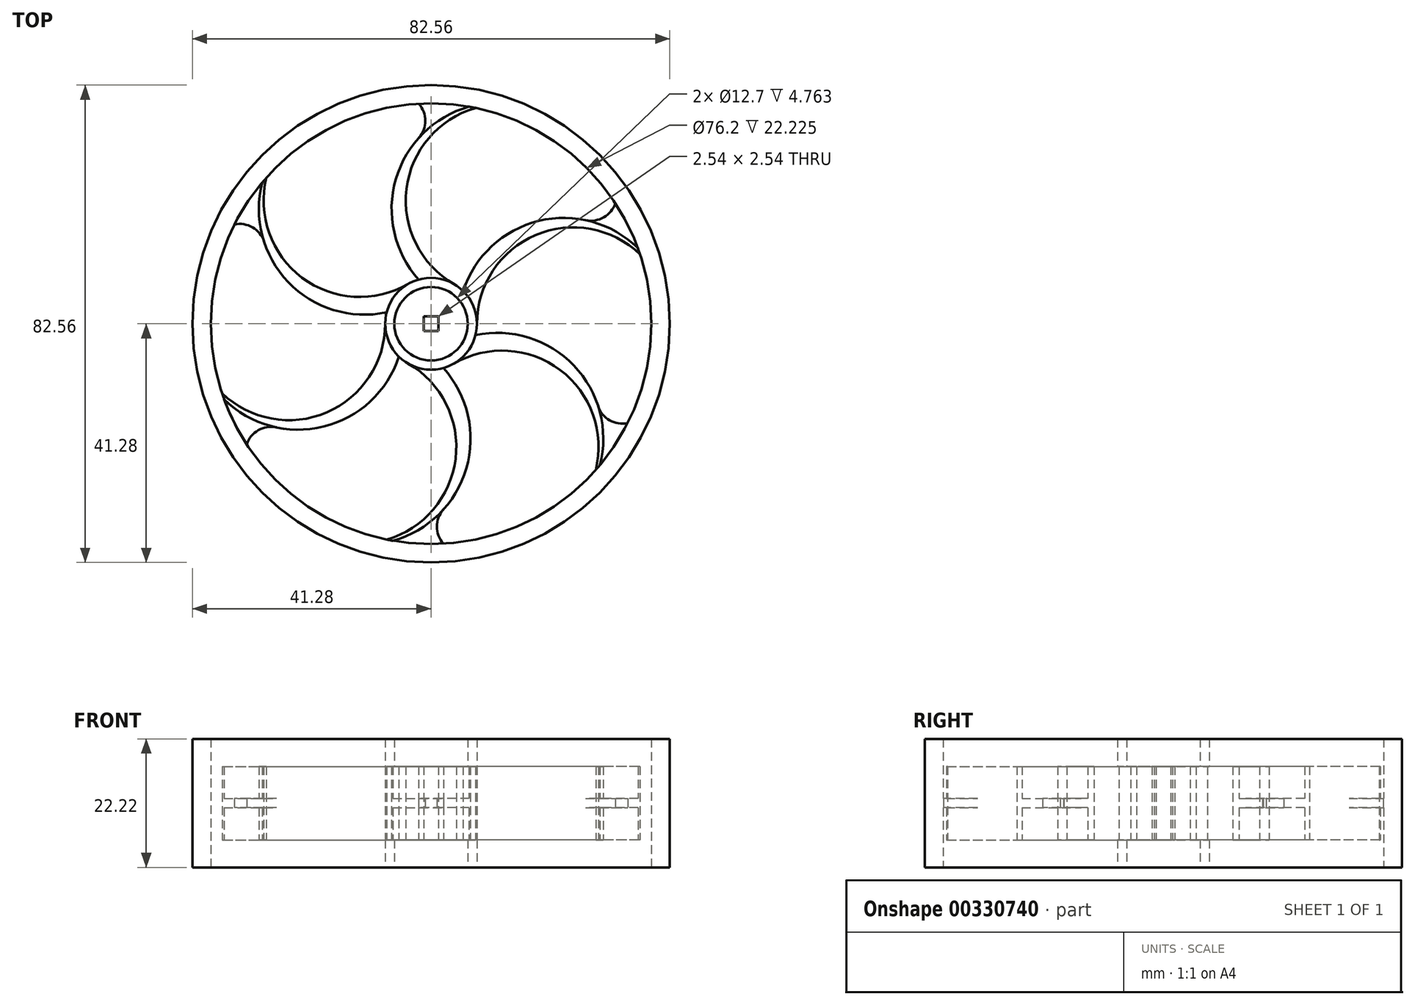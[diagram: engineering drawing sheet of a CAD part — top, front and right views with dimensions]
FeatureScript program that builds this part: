
annotation { "Feature Type Name" : "Feature", "Feature Type Description" : "" }
export const myFeature = defineFeature(function(context is Context, id is Id, definition is map)
    precondition{}
    {
        {
            var Q0;
            Q0=qCreatedBy(makeId("Top.planeOp"),FACE);
            var sketch = newSketch(context, id + "F0", { "sketchPlane" : qUnion([Q0])});
            skCircle(sketch, "E0", {"center": v(0, 0) * mm, "radius": 50.8 * mm});
            skCircle(sketch, "E1", {"center": v(0, 0) * mm, "radius": 41.28 * mm});
            skCircle(sketch, "E2", {"center": v(0, 0) * mm, "radius": 7.94 * mm});
            skLineSegment(sketch, "E3.bottom", {"start": v(-1.27, 1.27) * mm, "end": v(1.27, 1.27) * mm});
            skLineSegment(sketch, "E3.top", {"start": v(-1.27, -1.27) * mm, "end": v(1.27, -1.27) * mm});
            skLineSegment(sketch, "E3.left", {"start": v(-1.27, 1.27) * mm, "end": v(-1.27, -1.27) * mm});
            skLineSegment(sketch, "E3.right", {"start": v(1.27, 1.27) * mm, "end": v(1.27, -1.27) * mm});
            skLineSegment(sketch, "E4", {"start": v(-7.94, 0) * mm, "end": v(-41.28, 0) * mm, "construction": true});
            skLineSegment(sketch, "E5", {"start": v(7.94, 0) * mm, "end": v(41.28, 0) * mm, "construction": true});
            skArc(sketch, "E6", {"start": v(-41.28, 0) * mm, "mid": v(-24.6, -16.67) * mm, "end": v(-7.94, 0) * mm});
            skArc(sketch, "E7.1.0", {"start": v(-20.64, -35.75) * mm, "mid": v(2.13, -29.64) * mm, "end": v(-3.97, -6.87) * mm});
            skArc(sketch, "E7.2.0", {"start": v(20.64, -35.75) * mm, "mid": v(26.74, -12.98) * mm, "end": v(3.97, -6.87) * mm});
            skArc(sketch, "E7.3.0", {"start": v(41.28, 0) * mm, "mid": v(24.6, 16.67) * mm, "end": v(7.94, 0) * mm});
            skArc(sketch, "E7.4.0", {"start": v(20.64, 35.75) * mm, "mid": v(-2.13, 29.64) * mm, "end": v(3.97, 6.87) * mm});
            skArc(sketch, "E7.5.0", {"start": v(-20.64, 35.75) * mm, "mid": v(-26.74, 12.98) * mm, "end": v(-3.97, 6.87) * mm});
            skPoint(sketch, "E8", {"position": v(-2.13, 7.65) * mm});
            skPoint(sketch, "E8.positionSnap0", {"position": v(-2.13, 29.64) * mm});
            skPoint(sketch, "E9.1.0", {"position": v(-7.69, 1.98) * mm});
            skPoint(sketch, "E9.2.0", {"position": v(-5.56, -5.67) * mm});
            skPoint(sketch, "E9.3.0", {"position": v(2.13, -7.65) * mm});
            skPoint(sketch, "E9.4.0", {"position": v(7.69, -1.98) * mm});
            skPoint(sketch, "E9.5.0", {"position": v(5.56, 5.67) * mm});
            skArc(sketch, "E10", {"start": v(20.64, 35.75) * mm, "mid": v(-2.74, 31.42) * mm, "end": v(-2.13, 7.65) * mm});
            skArc(sketch, "E11.1.0", {"start": v(-20.64, 35.75) * mm, "mid": v(-28.58, 13.33) * mm, "end": v(-7.69, 1.98) * mm});
            skArc(sketch, "E11.2.0", {"start": v(-41.28, 0) * mm, "mid": v(-25.84, -18.08) * mm, "end": v(-5.56, -5.67) * mm});
            skArc(sketch, "E11.3.0", {"start": v(-20.64, -35.75) * mm, "mid": v(2.74, -31.42) * mm, "end": v(2.13, -7.65) * mm});
            skArc(sketch, "E11.4.0", {"start": v(20.64, -35.75) * mm, "mid": v(28.58, -13.33) * mm, "end": v(7.69, -1.98) * mm});
            skArc(sketch, "E11.5.0", {"start": v(41.28, 0) * mm, "mid": v(25.84, 18.08) * mm, "end": v(5.56, 5.67) * mm});
            skCircle(sketch, "E12", {"center": v(0, 0) * mm, "radius": 38.1 * mm});
            skCircle(sketch, "E13", {"center": v(0, 0) * mm, "radius": 6.35 * mm});
            skLineSegment(sketch, "E14", {"start": v(-2.13, 7.65) * mm, "end": v(-2.13, 38.04) * mm, "construction": true});
            skArc(sketch, "E15", {"start": v(-2.13, 32.13) * mm, "mid": v(-1, 35.09) * mm, "end": v(-2.13, 38.04) * mm});
            skArc(sketch, "E16.1.0", {"start": v(-28.9, 14.22) * mm, "mid": v(-30.88, 16.68) * mm, "end": v(-34.01, 17.17) * mm});
            skArc(sketch, "E16.2.0", {"start": v(-26.76, -17.91) * mm, "mid": v(-29.89, -18.4) * mm, "end": v(-31.88, -20.87) * mm});
            skArc(sketch, "E16.3.0", {"start": v(2.13, -32.13) * mm, "mid": v(1, -35.09) * mm, "end": v(2.13, -38.04) * mm});
            skArc(sketch, "E16.4.0", {"start": v(28.9, -14.22) * mm, "mid": v(30.88, -16.68) * mm, "end": v(34.01, -17.17) * mm});
            skArc(sketch, "E16.5.0", {"start": v(26.76, 17.91) * mm, "mid": v(29.89, 18.4) * mm, "end": v(31.88, 20.87) * mm});
            skSolve(sketch);
        }
        {
            var Q0;
            {var subQ3=sQuery(id+"F0.wireOp",EDGE,"E7.1.0");var subQ5=sQuery(id+"F0.wireOp",EDGE,"E12");var subQ7=makeQuery(id+"F0.imprint","INTERSECT",VERTEX,{"derivedFrom":[subQ3,subQ5]});Q0=makeQuery(id+"F0.imprint","IMPRINT",FACE,{"disambiguationData":[TD([[makeQuery(id+"F0.imprint","IMPRINT",EDGE,{"disambiguationData":[TD([[subQ7,1.0]])],"derivedFrom":subQ5}),-1.0]])]});}
            var Q1;
            {var subQ0=sQuery(id+"F0.wireOp",EDGE,"E6");var subQ5=sQuery(id+"F0.wireOp",EDGE,"E12");var subQ6=makeQuery(id+"F0.imprint","INTERSECT",VERTEX,{"derivedFrom":[subQ0,subQ5]});Q1=makeQuery(id+"F0.imprint","IMPRINT",FACE,{"disambiguationData":[TD([[makeQuery(id+"F0.imprint","IMPRINT",EDGE,{"disambiguationData":[TD([[subQ6,1.0]])],"derivedFrom":subQ5}),-1.0]])]});}
            var Q2;
            {var subQ3=sQuery(id+"F0.wireOp",EDGE,"E7.2.0");var subQ5=sQuery(id+"F0.wireOp",EDGE,"E12");var subQ6=makeQuery(id+"F0.imprint","INTERSECT",VERTEX,{"derivedFrom":[subQ3,subQ5]});Q2=makeQuery(id+"F0.imprint","IMPRINT",FACE,{"disambiguationData":[TD([[makeQuery(id+"F0.imprint","IMPRINT",EDGE,{"disambiguationData":[TD([[subQ6,1.0]])],"derivedFrom":subQ5}),-1.0]])]});}
            var Q3;
            {var subQ3=sQuery(id+"F0.wireOp",EDGE,"E7.4.0");var subQ5=sQuery(id+"F0.wireOp",EDGE,"E12");var subQ6=makeQuery(id+"F0.imprint","INTERSECT",VERTEX,{"derivedFrom":[subQ3,subQ5]});Q3=makeQuery(id+"F0.imprint","IMPRINT",FACE,{"disambiguationData":[TD([[makeQuery(id+"F0.imprint","IMPRINT",EDGE,{"disambiguationData":[TD([[subQ6,1.0]])],"derivedFrom":subQ5}),-1.0]])]});}
            var Q4;
            {var subQ3=sQuery(id+"F0.wireOp",EDGE,"E7.5.0");var subQ5=sQuery(id+"F0.wireOp",EDGE,"E12");var subQ6=makeQuery(id+"F0.imprint","INTERSECT",VERTEX,{"derivedFrom":[subQ3,subQ5]});Q4=makeQuery(id+"F0.imprint","IMPRINT",FACE,{"disambiguationData":[TD([[makeQuery(id+"F0.imprint","IMPRINT",EDGE,{"disambiguationData":[TD([[subQ6,1.0]])],"derivedFrom":subQ5}),-1.0]])]});}
            var Q5;
            {var subQ1=sQuery(id+"F0.wireOp",EDGE,"E7.5.0");var subQ3=sQuery(id+"F0.wireOp",EDGE,"E12");var subQ4=makeQuery(id+"F0.imprint","INTERSECT",VERTEX,{"derivedFrom":[subQ1,subQ3]});Q5=makeQuery(id+"F0.imprint","IMPRINT",FACE,{"disambiguationData":[TD([[makeQuery(id+"F0.imprint","IMPRINT",EDGE,{"disambiguationData":[TD([[subQ4,-1.0]])],"derivedFrom":subQ3}),-1.0]])]});}
            var Q6;
            {var subQ1=sQuery(id+"F0.wireOp",EDGE,"E7.4.0");var subQ3=sQuery(id+"F0.wireOp",EDGE,"E12");var subQ4=makeQuery(id+"F0.imprint","INTERSECT",VERTEX,{"derivedFrom":[subQ1,subQ3]});Q6=makeQuery(id+"F0.imprint","IMPRINT",FACE,{"disambiguationData":[TD([[makeQuery(id+"F0.imprint","IMPRINT",EDGE,{"disambiguationData":[TD([[subQ4,-1.0]])],"derivedFrom":subQ3}),-1.0]])]});}
            var Q7;
            {var subQ1=sQuery(id+"F0.wireOp",EDGE,"E7.3.0");var subQ3=sQuery(id+"F0.wireOp",EDGE,"E12");var subQ4=makeQuery(id+"F0.imprint","INTERSECT",VERTEX,{"derivedFrom":[subQ1,subQ3]});Q7=makeQuery(id+"F0.imprint","IMPRINT",FACE,{"disambiguationData":[TD([[makeQuery(id+"F0.imprint","IMPRINT",EDGE,{"disambiguationData":[TD([[subQ4,-1.0]])],"derivedFrom":subQ3}),-1.0]])]});}
            var Q8;
            {var subQ1=sQuery(id+"F0.wireOp",EDGE,"E7.2.0");var subQ3=sQuery(id+"F0.wireOp",EDGE,"E12");var subQ4=makeQuery(id+"F0.imprint","INTERSECT",VERTEX,{"derivedFrom":[subQ1,subQ3]});Q8=makeQuery(id+"F0.imprint","IMPRINT",FACE,{"disambiguationData":[TD([[makeQuery(id+"F0.imprint","IMPRINT",EDGE,{"disambiguationData":[TD([[subQ4,-1.0]])],"derivedFrom":subQ3}),-1.0]])]});}
            var Q9;
            {var subQ3=sQuery(id+"F0.wireOp",EDGE,"E7.3.0");var subQ5=sQuery(id+"F0.wireOp",EDGE,"E12");var subQ6=makeQuery(id+"F0.imprint","INTERSECT",VERTEX,{"derivedFrom":[subQ3,subQ5]});Q9=makeQuery(id+"F0.imprint","IMPRINT",FACE,{"disambiguationData":[TD([[makeQuery(id+"F0.imprint","IMPRINT",EDGE,{"disambiguationData":[TD([[subQ6,1.0]])],"derivedFrom":subQ5}),-1.0]])]});}
            var Q10;
            {var subQ1=sQuery(id+"F0.wireOp",EDGE,"E7.1.0");var subQ3=sQuery(id+"F0.wireOp",EDGE,"E12");var subQ4=makeQuery(id+"F0.imprint","INTERSECT",VERTEX,{"derivedFrom":[subQ1,subQ3]});Q10=makeQuery(id+"F0.imprint","IMPRINT",FACE,{"disambiguationData":[TD([[makeQuery(id+"F0.imprint","IMPRINT",EDGE,{"disambiguationData":[TD([[subQ4,-1.0]])],"derivedFrom":subQ3}),-1.0]])]});}
            var Q11;
            {var subQ1=sQuery(id+"F0.wireOp",EDGE,"E6");var subQ3=sQuery(id+"F0.wireOp",EDGE,"E12");var subQ4=makeQuery(id+"F0.imprint","INTERSECT",VERTEX,{"derivedFrom":[subQ1,subQ3]});Q11=makeQuery(id+"F0.imprint","IMPRINT",FACE,{"disambiguationData":[TD([[makeQuery(id+"F0.imprint","IMPRINT",EDGE,{"disambiguationData":[TD([[subQ4,-1.0]])],"derivedFrom":subQ3}),-1.0]])]});}
            extrude(context, id + "F1", {"entities" : qUnion([Q0, Q1, Q2, Q3, Q4, Q5, Q6, Q7, Q8, Q9, Q10, Q11]), "depth" : 22.22 * mm, "symmetric" : true});
        }
        {
            var Q0;
            {var subQ0=sQuery(id+"F0.wireOp",EDGE,"E7.5.0");var subQ1=sQuery(id+"F0.wireOp",EDGE,"E2");var subQ2=makeQuery(id+"F0.imprint","INTERSECT",VERTEX,{"derivedFrom":[subQ1,subQ0]});Q0=makeQuery(id+"F0.imprint","IMPRINT",FACE,{"disambiguationData":[TD([[makeQuery(id+"F0.imprint","IMPRINT",EDGE,{"disambiguationData":[TD([[subQ2,-1.0]])],"derivedFrom":subQ1}),-1.0]])]});}
            var Q1;
            {var subQ0=sQuery(id+"F0.wireOp",EDGE,"E7.4.0");var subQ1=sQuery(id+"F0.wireOp",EDGE,"E2");var subQ2=makeQuery(id+"F0.imprint","INTERSECT",VERTEX,{"derivedFrom":[subQ1,subQ0]});Q1=makeQuery(id+"F0.imprint","IMPRINT",FACE,{"disambiguationData":[TD([[makeQuery(id+"F0.imprint","IMPRINT",EDGE,{"disambiguationData":[TD([[subQ2,-1.0]])],"derivedFrom":subQ1}),-1.0]])]});}
            var Q2;
            {var subQ0=sQuery(id+"F0.wireOp",EDGE,"E7.3.0");var subQ1=sQuery(id+"F0.wireOp",EDGE,"E2");var subQ2=makeQuery(id+"F0.imprint","INTERSECT",VERTEX,{"derivedFrom":[subQ1,subQ0]});Q2=makeQuery(id+"F0.imprint","IMPRINT",FACE,{"disambiguationData":[TD([[makeQuery(id+"F0.imprint","IMPRINT",EDGE,{"disambiguationData":[TD([[subQ2,-1.0]])],"derivedFrom":subQ1}),-1.0]])]});}
            var Q3;
            {var subQ0=sQuery(id+"F0.wireOp",EDGE,"E7.2.0");var subQ1=sQuery(id+"F0.wireOp",EDGE,"E2");var subQ2=makeQuery(id+"F0.imprint","INTERSECT",VERTEX,{"derivedFrom":[subQ1,subQ0]});Q3=makeQuery(id+"F0.imprint","IMPRINT",FACE,{"disambiguationData":[TD([[makeQuery(id+"F0.imprint","IMPRINT",EDGE,{"disambiguationData":[TD([[subQ2,-1.0]])],"derivedFrom":subQ1}),-1.0]])]});}
            var Q4;
            {var subQ0=sQuery(id+"F0.wireOp",EDGE,"E7.1.0");var subQ1=sQuery(id+"F0.wireOp",EDGE,"E2");var subQ2=makeQuery(id+"F0.imprint","INTERSECT",VERTEX,{"derivedFrom":[subQ1,subQ0]});Q4=makeQuery(id+"F0.imprint","IMPRINT",FACE,{"disambiguationData":[TD([[makeQuery(id+"F0.imprint","IMPRINT",EDGE,{"disambiguationData":[TD([[subQ2,-1.0]])],"derivedFrom":subQ1}),-1.0]])]});}
            var Q5;
            {var subQ0=sQuery(id+"F0.wireOp",EDGE,"E6");var subQ1=sQuery(id+"F0.wireOp",EDGE,"E2");var subQ2=makeQuery(id+"F0.imprint","INTERSECT",VERTEX,{"derivedFrom":[subQ1,subQ0]});Q5=makeQuery(id+"F0.imprint","IMPRINT",FACE,{"disambiguationData":[TD([[makeQuery(id+"F0.imprint","IMPRINT",EDGE,{"disambiguationData":[TD([[subQ2,-1.0]])],"derivedFrom":subQ1}),-1.0]])]});}
            extrude(context, id + "F2", {"entities" : qUnion([Q0, Q1, Q2, Q3, Q4, Q5]), "operationType" : NewBodyOperationType.ADD, "depth" : 12.7 * mm, "symmetric" : true});
        }
        {
            var Q0;
            Q0=makeQuery(id+"F0.imprint","IMPRINT",FACE,{"disambiguationData":[TD([[makeQuery(id+"F0.imprint","IMPRINT",EDGE,{"derivedFrom":sQuery(id+"F0.wireOp",EDGE,"E13")}),-1.0]])]});
            extrude(context, id + "F3", {"entities" : qUnion([Q0]), "operationType" : NewBodyOperationType.ADD, "depth" : 22.22 * mm, "symmetric" : true});
        }
        {
            var Q0;
            Q0=makeQuery(id+"F0.imprint","IMPRINT",FACE,{"disambiguationData":[TD([[makeQuery(id+"F0.imprint","IMPRINT",EDGE,{"derivedFrom":sQuery(id+"F0.wireOp",EDGE,"E3.bottom")}),1.0]])]});
            extrude(context, id + "F4", {"entities" : qUnion([Q0]), "operationType" : NewBodyOperationType.ADD, "depth" : 12.7 * mm, "symmetric" : true});
        }
        {
            var Q0;
            {var subQ0=sQuery(id+"F0.wireOp",EDGE,"E16.1.0");Q0=makeQuery(id+"F0.imprint","IMPRINT",FACE,{"disambiguationData":[TD([[makeQuery(id+"F0.imprint","IMPRINT",EDGE,{"derivedFrom":subQ0}),-1.0]])]});}
            var Q1;
            {var subQ0=sQuery(id+"F0.wireOp",EDGE,"E15");Q1=makeQuery(id+"F0.imprint","IMPRINT",FACE,{"disambiguationData":[TD([[makeQuery(id+"F0.imprint","IMPRINT",EDGE,{"derivedFrom":subQ0}),-1.0]])]});}
            var Q2;
            {var subQ0=sQuery(id+"F0.wireOp",EDGE,"E16.5.0");Q2=makeQuery(id+"F0.imprint","IMPRINT",FACE,{"disambiguationData":[TD([[makeQuery(id+"F0.imprint","IMPRINT",EDGE,{"derivedFrom":subQ0}),-1.0]])]});}
            var Q3;
            {var subQ0=sQuery(id+"F0.wireOp",EDGE,"E16.4.0");Q3=makeQuery(id+"F0.imprint","IMPRINT",FACE,{"disambiguationData":[TD([[makeQuery(id+"F0.imprint","IMPRINT",EDGE,{"derivedFrom":subQ0}),-1.0]])]});}
            var Q4;
            {var subQ0=sQuery(id+"F0.wireOp",EDGE,"E16.3.0");Q4=makeQuery(id+"F0.imprint","IMPRINT",FACE,{"disambiguationData":[TD([[makeQuery(id+"F0.imprint","IMPRINT",EDGE,{"derivedFrom":subQ0}),-1.0]])]});}
            var Q5;
            {var subQ0=sQuery(id+"F0.wireOp",EDGE,"E16.2.0");Q5=makeQuery(id+"F0.imprint","IMPRINT",FACE,{"disambiguationData":[TD([[makeQuery(id+"F0.imprint","IMPRINT",EDGE,{"derivedFrom":subQ0}),-1.0]])]});}
            extrude(context, id + "F5", {"entities" : qUnion([Q0, Q1, Q2, Q3, Q4, Q5]), "operationType" : NewBodyOperationType.ADD, "depth" : 1.59 * mm, "symmetric" : true});
        }
    });
